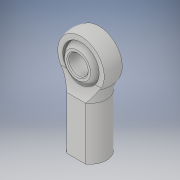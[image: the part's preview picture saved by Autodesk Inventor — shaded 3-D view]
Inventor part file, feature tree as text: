
AUTODESK INVENTOR PART (.ipt)
format: ipt  version: 2017 (Build 210142000, 142)  size: 730,624 bytes
history: native  units: in
note: dims shown in document units (in); Inventor stores cm internally (conversion verified against a paired STEP export)
features: other x2, chamfer x1
ambient origin geometry x8: Origin, YZ Plane, XZ Plane, XY Plane, X Axis, Y Axis, Z Axis, Center Point
bodies: Solid1 (feature_tree), Solid2 (feature_tree)
feature tree (3):
  other  "60645K351_STEEL BALL JOINT ROD END1"
  other  "Cut-Extrude2"
  chamfer  "Chamfer1"  [1 undecoded]
note: 1 required parameter value undecoded (feature->parameter linkage not recoverable at this tier; creation-order binding heuristic only, values carry confidence <= 0.55)
